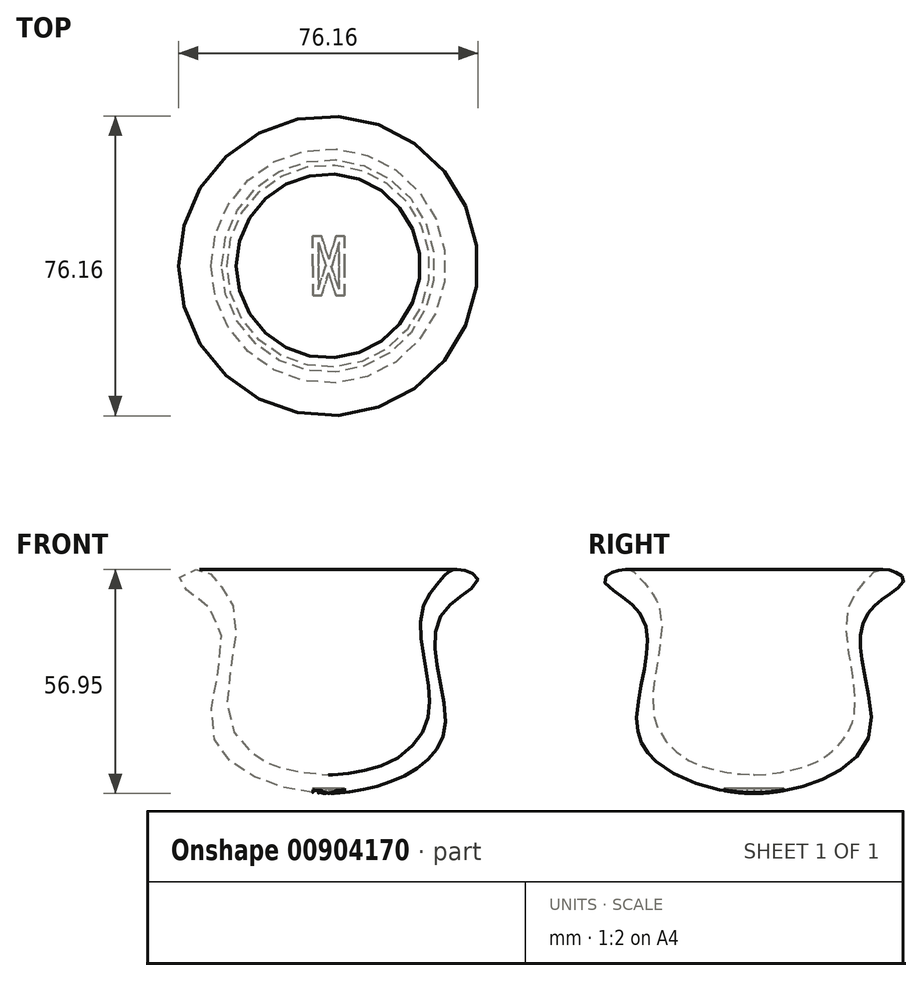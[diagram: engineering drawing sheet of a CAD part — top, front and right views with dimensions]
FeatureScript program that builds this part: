
annotation { "Feature Type Name" : "Feature", "Feature Type Description" : "" }
export const myFeature = defineFeature(function(context is Context, id is Id, definition is map)
    precondition{}
    {
        {
            var Q0;
            Q0=qCreatedBy(makeId("Front.planeOp"),FACE);
            var sketch = newSketch(context, id + "F0", { "sketchPlane" : qUnion([Q0])});
            skLineSegment(sketch, "E0", {"start": v(-31.75, 0) * mm, "end": v(31.75, 0) * mm, "construction": true});
            skLineSegment(sketch, "E1", {"start": v(0, 0) * mm, "end": v(0, -50.8) * mm, "construction": true});
            skLineSegment(sketch, "E2", {"start": v(-12.7, -50.8) * mm, "end": v(12.7, -50.8) * mm, "construction": true});
            skLineSegment(sketch, "E3", {"start": v(0, 0) * mm, "end": v(0, -12.7) * mm, "construction": true});
            skLineSegment(sketch, "E4", {"start": v(-23.5, -12.7) * mm, "end": v(23.5, -12.7) * mm, "construction": true});
            skLineSegment(sketch, "E5", {"start": v(0, -50.8) * mm, "end": v(0, -38.1) * mm, "construction": true});
            skLineSegment(sketch, "E6", {"start": v(-25.4, -38.1) * mm, "end": v(25.4, -38.1) * mm, "construction": true});
            skLineSegment(sketch, "E7", {"start": v(0, -52.8) * mm, "end": v(0, -57.57) * mm, "construction": true});
            skLineSegment(sketch, "E8", {"start": v(-19.77, -52.8) * mm, "end": v(-17.38, -48.69) * mm, "construction": true});
            skLineSegment(sketch, "E9", {"start": v(-28.25, -13.02) * mm, "end": v(-23.5, -12.7) * mm, "construction": true});
            skLineSegment(sketch, "E10", {"start": v(23.5, -12.7) * mm, "end": v(28.25, -12.93) * mm, "construction": true});
            skLineSegment(sketch, "E11", {"start": v(-25.4, -38.1) * mm, "end": v(-29.76, -40.01) * mm, "construction": true});
            skLineSegment(sketch, "E12", {"start": v(25.4, -38.1) * mm, "end": v(30.07, -39.03) * mm, "construction": true});
            skLineSegment(sketch, "E13", {"start": v(16.77, -49.02) * mm, "end": v(19.05, -53.2) * mm, "construction": true});
            skLineSegment(sketch, "E14", {"start": v(-31.75, 0) * mm, "end": v(-38.08, -3.3) * mm, "construction": true});
            skLineSegment(sketch, "E15", {"start": v(31.75, 0) * mm, "end": v(37.76, -3.85) * mm, "construction": true});
            skLineSegment(sketch, "E16", {"start": v(0, -52.8) * mm, "end": v(0, -57.57) * mm});
            skLineSegment(sketch, "E17", {"start": v(0, -57.57) * mm, "end": v(-12.7, -57.57) * mm, "construction": true});
            skLineSegment(sketch, "E18", {"start": v(0, -57.57) * mm, "end": v(12.7, -57.57) * mm, "construction": true});
            skLineSegment(sketch, "E19", {"start": v(-12.7, -57.57) * mm, "end": v(12.7, -57.57) * mm});
            skLineSegment(sketch, "E20", {"start": v(-12.7, -57.57) * mm, "end": v(-12.7, -58.84) * mm});
            skLineSegment(sketch, "E21", {"start": v(-12.7, -58.84) * mm, "end": v(12.7, -58.84) * mm});
            skLineSegment(sketch, "E22", {"start": v(12.7, -58.84) * mm, "end": v(12.7, -57.57) * mm});
            skLineSegment(sketch, "E23", {"start": v(-28.58, -3.3) * mm, "end": v(28.57, -3.3) * mm, "construction": true});
            skLineSegment(sketch, "E24", {"start": v(-32.45, -0.62) * mm, "end": v(31.8, -0.62) * mm, "construction": true});
            skFitSpline(sketch, "E25", {"points": [v(0, -57.57) * mm, v(-19.77, -52.8) * mm, v(-29.76, -40.01) * mm, v(-28.25, -13.02) * mm, v(-38.08, -3.3) * mm, v(-32.45, -0.62) * mm, v(-28.58, -3.3) * mm, v(-23.5, -12.7) * mm, v(-25.4, -38.1) * mm, v(-17.38, -48.69) * mm, v(-12.7, -50.8) * mm, v(0, -52.8) * mm, v(12.7, -50.8) * mm, v(16.77, -49.02) * mm, v(25.4, -38.1) * mm, v(23.5, -12.7) * mm, v(28.58, -3.3) * mm, v(31.8, -0.62) * mm, v(37.76, -3.85) * mm, v(28.25, -12.93) * mm, v(30.07, -39.03) * mm, v(19.05, -53.2) * mm, v(0, -57.57) * mm]});
            skLineSegment(sketch, "E26", {"start": v(0, 0) * mm, "end": v(0, -3.3) * mm, "construction": true});
            skSolve(sketch);
        }
        {
            var Q0;
            {var subQ0=sQuery(id+"F0.wireOp",EDGE,"E16");Q0=makeQuery(id+"F0.imprint","IMPRINT",FACE,{"disambiguationData":[TD([[makeQuery(id+"F0.imprint","IMPRINT",EDGE,{"derivedFrom":subQ0}),-1.0]])]});}
            var Q1;
            Q1=sQuery(id+"F0.wireOp",EDGE,"E3");
            revolve(context, id + "F1", {"surfaceOperationType" : NewSurfaceOperationType.NEW, "entities" : qUnion([Q0]), "axis" : qUnion([Q1]), "revolveType" : RevolveType.FULL});
        }
        {
            var Q0;
            {var subQ0=sQuery(id+"F0.wireOp",EDGE,"E20");Q0=makeQuery(id+"F0.imprint","IMPRINT",FACE,{"disambiguationData":[TD([[makeQuery(id+"F0.imprint","IMPRINT",EDGE,{"derivedFrom":subQ0}),1.0]])]});}
            extrude(context, id + "F2", {"entities" : qUnion([Q0]), "endBound" : BoundingType.SYMMETRIC, "depth" : 25.4 * mm, "offsetDistance" : 25.4 * mm});
        }
        {
            var Q0;
            Q0=makeQuery(id+"F2.opExtrude","SWEPT_FACE",FACE,{"disambiguationData":[OSD([sQuery(id+"F0.wireOp",EDGE,"E21")])]});
            var sketch = newSketch(context, id + "F3", { "sketchPlane" : qUnion([Q0])});
            skText(sketch, "E27", { "text": "M", "fontName": "OpenSans-Bold.ttf"});
            skText(sketch, "E28", { "text": "M", "fontName": "OpenSans-Bold.ttf"});
            const initialGuessF3  = {"E27": [-0.00487, 0, 1, 0, 0.00764], "E28": [0.00512, 0, -1, 0, 0.00764]};
            skSetInitialGuess(sketch, initialGuessF3);
            skSolve(sketch);
        }
        {
            var Q0;
            Q0=makeQuery(id+"F3.imprint","IMPRINT",FACE,{"disambiguationData":[TD([[makeQuery(id+"F3.imprint","IMPRINT",EDGE,{"derivedFrom":sQuery(id+"F3.wireOp",EDGE,"E28.sketch_text.stroke-0")}),-1.0]])]});
            var Q1;
            Q1=makeQuery(id+"F3.imprint","IMPRINT",FACE,{"disambiguationData":[TD([[makeQuery(id+"F3.imprint","IMPRINT",EDGE,{"derivedFrom":sQuery(id+"F3.wireOp",EDGE,"E27.sketch_text.stroke-0")}),-1.0]])]});
            extrude(context, id + "F4", {"entities" : qUnion([Q0, Q1]), "operationType" : NewBodyOperationType.REMOVE, "oppositeDirection" : true, "depth" : 2.54 * mm, "offsetDistance" : 25.4 * mm});
        }
        {
            var Q0;
            Q0=makeQuery(id+"F2.opExtrude","CAP_FACE",FACE,{"disambiguationData":[OSD([sQuery(id+"F0.wireOp",EDGE,"e4397e48-d3bc-4ec0-b99d-247f3e213b33"),sQuery(id+"F0.wireOp",EDGE,"E19"),sQuery(id+"F0.wireOp",EDGE,"E20"),sQuery(id+"F0.wireOp",EDGE,"E21"),sQuery(id+"F0.wireOp",EDGE,"E22")])],"isStart":false});
            extrude(context, id + "F5", {"entities" : qUnion([Q0]), "operationType" : NewBodyOperationType.REMOVE, "endBound" : BoundingType.THROUGH_ALL, "oppositeDirection" : true, "depth" : 25.4 * mm, "offsetDistance" : 25.4 * mm});
        }
    });
